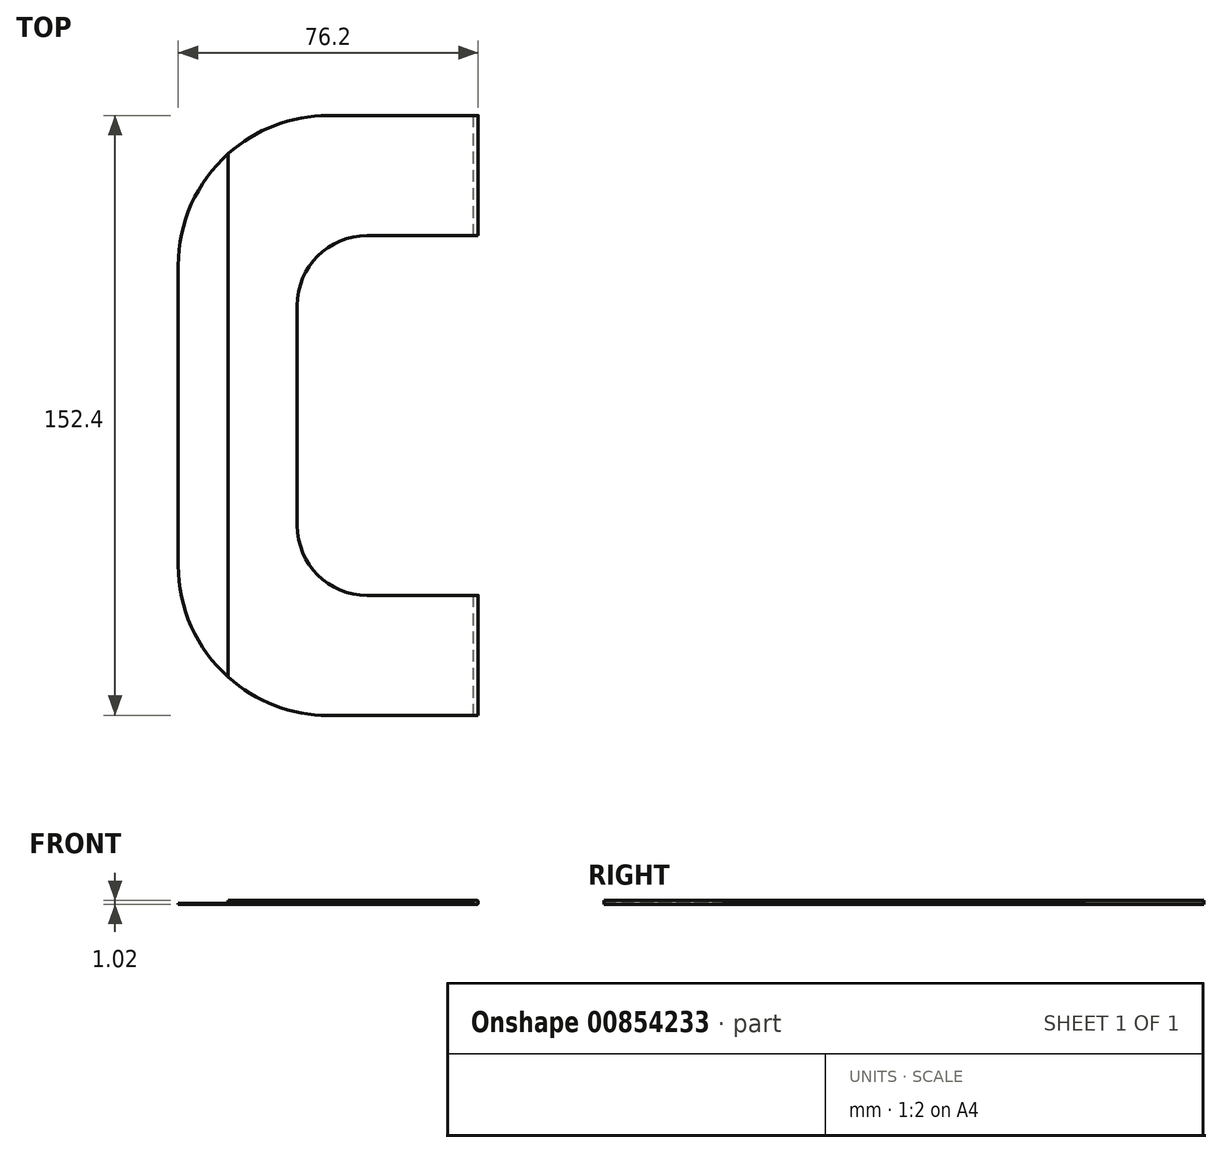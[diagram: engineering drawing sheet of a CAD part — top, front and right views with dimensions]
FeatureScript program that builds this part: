
annotation { "Feature Type Name" : "Feature", "Feature Type Description" : "" }
export const myFeature = defineFeature(function(context is Context, id is Id, definition is map)
    precondition{}
    {
        {
            var Q0;
            Q0=qCreatedBy(makeId("Top.planeOp"),FACE);
            var sketch = newSketch(context, id + "F0", { "sketchPlane" : qUnion([Q0])});
            skLineSegment(sketch, "E0.bottom", {"start": v(0, 93) * mm, "end": v(-38.1, 93) * mm});
            skLineSegment(sketch, "E0.top", {"start": v(0, -59.4) * mm, "end": v(-38.1, -59.4) * mm});
            skLineSegment(sketch, "E0.left", {"start": v(0, 93) * mm, "end": v(0, -59.4) * mm});
            skLineSegment(sketch, "E0.right", {"start": v(-76.2, 54.9) * mm, "end": v(-76.2, -21.3) * mm});
            skPoint(sketch, "E1.visualSharp", {"position": v(-76.2, 93) * mm});
            skArc(sketch, "E1.filletArc", {"start": v(-38.1, 93) * mm, "mid": v(-65.04, 81.85) * mm, "end": v(-76.2, 54.9) * mm});
            skPoint(sketch, "E2.visualSharp", {"position": v(-76.2, -59.4) * mm});
            skArc(sketch, "E2.filletArc", {"start": v(-76.2, -21.3) * mm, "mid": v(-65.04, -48.23) * mm, "end": v(-38.1, -59.4) * mm});
            skSolve(sketch);
        }
        {
            var Q0;
            Q0 = qSketchRegion(id + "F0", true);
            extrude(context, id + "F1", {"entities" : qUnion([Q0]), "depth" : 1.02 * mm, "offsetDistance" : 25.4 * mm});
        }
        {
            var Q0;
            Q0=makeQuery(id+"F1.opExtrude","SWEPT_FACE",FACE,{"disambiguationData":[OSD([sQuery(id+"F0.wireOp",EDGE,"E0.right")])]});
            var sketch = newSketch(context, id + "F2", { "sketchPlane" : qUnion([Q0])});
            skLineSegment(sketch, "E3.bottom", {"start": v(-98.4, 0.76) * mm, "end": v(61.62, 0.76) * mm});
            skLineSegment(sketch, "E3.top", {"start": v(-98.4, 0.25) * mm, "end": v(61.62, 0.25) * mm});
            skLineSegment(sketch, "E3.left", {"start": v(-98.4, 0.76) * mm, "end": v(-98.4, 0.25) * mm});
            skLineSegment(sketch, "E3.right", {"start": v(61.62, 0.76) * mm, "end": v(61.62, 0.25) * mm});
            skSolve(sketch);
        }
        {
            var Q0;
            Q0 = qSketchRegion(id + "F2", true);
            extrude(context, id + "F3", {"entities" : qUnion([Q0]), "operationType" : NewBodyOperationType.REMOVE, "oppositeDirection" : true, "depth" : 74.93 * mm, "offsetDistance" : 25.4 * mm});
        }
        {
            var Q0;
            Q0=makeQuery(id+"F1.opExtrude","CAP_FACE",FACE,{"disambiguationData":[OSD([sQuery(id+"F0.wireOp",EDGE,"E0.bottom"),sQuery(id+"F0.wireOp",EDGE,"E0.top"),sQuery(id+"F0.wireOp",EDGE,"E0.left"),sQuery(id+"F0.wireOp",EDGE,"E0.right"),sQuery(id+"F0.wireOp",EDGE,"E1.filletArc"),sQuery(id+"F0.wireOp",EDGE,"E2.filletArc")])],"isStart":false});
            var sketch = newSketch(context, id + "F4", { "sketchPlane" : qUnion([Q0])});
            skLineSegment(sketch, "E4.bottom", {"start": v(-98.2, 105.34) * mm, "end": v(-63.5, 105.34) * mm});
            skLineSegment(sketch, "E4.top", {"start": v(-98.2, -79.26) * mm, "end": v(-63.5, -79.26) * mm});
            skLineSegment(sketch, "E4.left", {"start": v(-98.2, 105.34) * mm, "end": v(-98.2, -79.26) * mm});
            skLineSegment(sketch, "E4.right", {"start": v(-63.5, 105.34) * mm, "end": v(-63.5, -79.26) * mm});
            skSolve(sketch);
        }
        {
            var Q0;
            Q0 = qSketchRegion(id + "F4", true);
            extrude(context, id + "F5", {"entities" : qUnion([Q0]), "operationType" : NewBodyOperationType.REMOVE, "oppositeDirection" : true, "depth" : 0.5 * mm, "offsetDistance" : 25.4 * mm});
        }
        {
            var Q0;
            Q0=makeQuery(id+"F1.opExtrude","CAP_EDGE",EDGE,{"disambiguationData":[OSD([sQuery(id+"F0.wireOp",EDGE,"E0.left")])],"isStart":false});
            fillet(context, id + "F6", {"entities" : qUnion([Q0]), "radius" : 0.25 * mm, "tangentPropagation" : true, "allowEdgeOverflow" : false});
        }
        {
            var Q0;
            Q0=makeQuery(id+"F1.opExtrude","CAP_EDGE",EDGE,{"disambiguationData":[OSD([sQuery(id+"F0.wireOp",EDGE,"E0.left")])],"isStart":true});
            fillet(context, id + "F7", {"entities" : qUnion([Q0]), "radius" : 0.25 * mm, "tangentPropagation" : true, "allowEdgeOverflow" : false});
        }
        {
            var Q0;
            Q0=makeQuery(id+"F1.opExtrude","CAP_FACE",FACE,{"disambiguationData":[OSD([sQuery(id+"F0.wireOp",EDGE,"E0.bottom"),sQuery(id+"F0.wireOp",EDGE,"E0.top"),sQuery(id+"F0.wireOp",EDGE,"E0.left"),sQuery(id+"F0.wireOp",EDGE,"E0.right"),sQuery(id+"F0.wireOp",EDGE,"E1.filletArc"),sQuery(id+"F0.wireOp",EDGE,"E2.filletArc")])],"isStart":false});
            var sketch = newSketch(context, id + "F8", { "sketchPlane" : qUnion([Q0])});
            skLineSegment(sketch, "E5.bottom", {"start": v(-28.2, 62.53) * mm, "end": v(40.76, 62.53) * mm});
            skLineSegment(sketch, "E5.top", {"start": v(-28.2, -28.91) * mm, "end": v(40.76, -28.91) * mm});
            skLineSegment(sketch, "E5.left", {"start": v(-45.97, 44.75) * mm, "end": v(-45.97, -11.13) * mm});
            skLineSegment(sketch, "E5.right", {"start": v(40.76, 62.53) * mm, "end": v(40.76, -28.91) * mm});
            skPoint(sketch, "E6.visualSharp", {"position": v(-45.97, 62.53) * mm});
            skArc(sketch, "E6.filletArc", {"start": v(-28.2, 62.53) * mm, "mid": v(-40.77, 57.32) * mm, "end": v(-45.97, 44.75) * mm});
            skPoint(sketch, "E7.visualSharp", {"position": v(-45.97, -28.91) * mm});
            skArc(sketch, "E7.filletArc", {"start": v(-45.97, -11.13) * mm, "mid": v(-40.77, -23.7) * mm, "end": v(-28.2, -28.91) * mm});
            skSolve(sketch);
        }
        {
            var Q0;
            Q0 = qSketchRegion(id + "F8", true);
            extrude(context, id + "F9", {"entities" : qUnion([Q0]), "operationType" : NewBodyOperationType.REMOVE, "endBound" : BoundingType.THROUGH_ALL, "oppositeDirection" : true, "depth" : 25.4 * mm, "offsetDistance" : 25.4 * mm});
        }
    });
